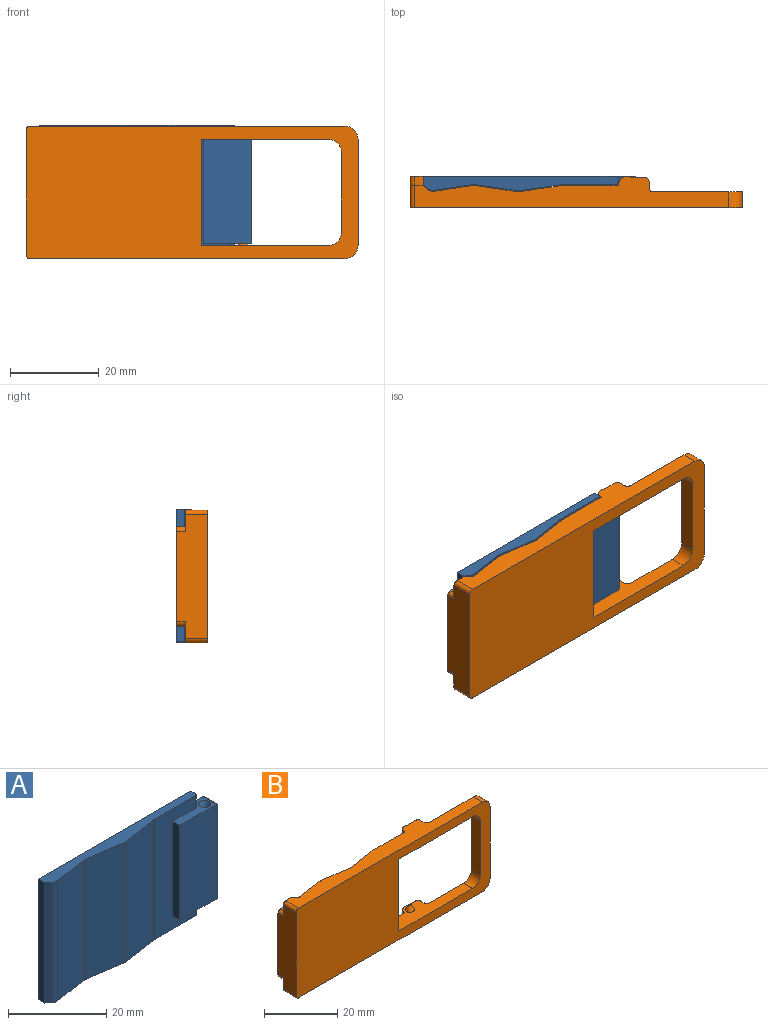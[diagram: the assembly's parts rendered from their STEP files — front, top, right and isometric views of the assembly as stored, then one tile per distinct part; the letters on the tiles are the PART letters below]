
ASSEMBLY  parts=2 mates=1
PART A: 26 faces, bbox 48x3.8x30 mm
  f0: plane 30x11.85mm, normal (0,-1,0), area 202.1mm2, adj f8,f9,f11,f13,f14,f20,f21,f22
  f1: plane 48x30mm, normal (0,1,0), area 1414.3mm2, adj f2,f7,f8,f9,f10,f11,f12,f13
  f2: plane 30x1.8mm, normal (-1,0,0), area 54mm2, adj f1,f3,f8,f9
  f3: plane 30x0.79mm, normal (-0.71,-0.71,0), area 33.4mm2, adj f2,f8,f9,f25
  f4: plane 30x8.71mm, normal (0.15,-0.99,0), area 264.1mm2, adj f8,f9,f24,f25
  f5: plane 30x9.41mm, normal (-0.15,-0.99,0), area 285.4mm2, adj f8,f9,f23,f24
  f6: plane 30x9.56mm, normal (0.15,-0.99,0), area 289.9mm2, adj f8,f9,f22,f23
  f7: plane 22.6x3.8mm, normal (1,0,0), area 85.9mm2, adj f1,f15,f18,f19
  f8: plane 44x3.28mm, normal (0,0,1), area 102.6mm2, adj f0,f1,f2,f3,f4,f5,f6,f10
  f9: plane 44x3.28mm, normal (0,0,-1), area 102.6mm2, adj f0,f1,f2,f3,f4,f5,f6,f12
  f10: plane 3.2x1.3mm, normal (1,0,0), area 4.2mm2, adj f1,f8,f11,f21
  f11: plane 10.5x3.8mm, normal (0,0,1), area 22.4mm2, adj f0,f1,f10,f14,f15,f17,f19,f21
  f12: plane 3.2x1.3mm, normal (1,0,0), area 4.2mm2, adj f1,f9,f13,f20
  f13: plane 10.5x3.8mm, normal (0,0,-1), area 22.4mm2, adj f0,f1,f12,f14,f15,f16,f18,f20
  f14: plane 23.6x2mm, normal (-1,0,0), area 47.2mm2, adj f0,f11,f13,f15
  f15: plane 23.6x11mm, normal (0,-1,0), area 259.5mm2, adj f7,f11,f13,f14,f18,f19
  f16: cone r=1.25mm half-angle=30deg, axis (0,0,-1), area 9.8mm2, adj f13
  f17: cone r=1.25mm half-angle=30deg, axis (0,0,1), area 9.8mm2, adj f11
  f18: cylinder r=0.5mm len=3.8mm, axis (0,-1,0), area 3mm2, adj f1,f7,f13,f15
  f19: cylinder r=0.5mm len=3.8mm, axis (0,-1,0), area 3mm2, adj f1,f7,f11,f15
  f20: cylinder r=0.5mm len=3.2mm, axis (0,0,-1), area 2.5mm2, adj f0,f9,f12,f13
  f21: cylinder r=0.5mm len=3.2mm, axis (0,0,-1), area 2.5mm2, adj f0,f8,f10,f11
  f22: cylinder r=2mm len=30mm, axis (0,0,1), area 8.9mm2, adj f0,f6,f8,f9
  f23: cylinder r=2mm len=30mm, axis (0,0,-1), area 17.9mm2, adj f5,f6,f8,f9
  f24: cylinder r=2mm len=30mm, axis (0,0,1), area 17.9mm2, adj f4,f5,f8,f9
  f25: cylinder r=2mm len=30mm, axis (0,0,-1), area 56.1mm2, adj f3,f4,f8,f9
PART B: 49 faces, bbox 75x7x30 mm
  f0: plane 28.5x7mm, normal (0,0,1), area 128.5mm2, adj f4,f5,f7,f9,f10,f19,f24,f32
  f1: plane 28.5x7mm, normal (0,0,-1), area 128.5mm2, adj f4,f5,f6,f8,f10,f19,f23,f31
  f2: plane 4.75x3mm, normal (0,1,0), area 11.3mm2, adj f11,f14,f15,f26,f27,f40
  f3: plane 4.75x3mm, normal (0,1,0), area 11.3mm2, adj f11,f12,f15,f28,f29,f39
  f4: plane 75x30mm, normal (0,-1,0), area 1493.6mm2, adj f0,f1,f11,f12,f13,f14,f19,f20
  f5: plane 30x12.35mm, normal (0,1,0), area 196.5mm2, adj f0,f1,f6,f7,f12,f14,f19,f45
  f6: cylinder r=2mm len=3mm, axis (0,0,1), area 12.1mm2, adj f1,f5,f12,f33
  f7: cylinder r=2mm len=3mm, axis (0,0,1), area 12.1mm2, adj f0,f5,f14,f34
  f8: plane 3x1.3mm, normal (1,0,0), area 3.9mm2, adj f1,f12,f41,f44
  f9: plane 3x1.3mm, normal (1,0,0), area 3.9mm2, adj f0,f14,f42,f43
  f10: plane 30x20mm, normal (0,1,0), area 210mm2, adj f0,f1,f12,f13,f14,f20,f21,f22
  f11: plane 28x7mm, normal (-1,0,0), area 181mm2, adj f2,f3,f4,f27,f28,f30,f39,f40
  f12: plane 71x7mm, normal (0,0,1), area 316.8mm2, adj f3,f4,f5,f6,f8,f10,f15,f16
  f13: plane 24x3.5mm, normal (1,0,0), area 84mm2, adj f4,f10,f21,f22
  f14: plane 71x7mm, normal (0,0,-1), area 316.8mm2, adj f2,f4,f5,f7,f9,f10,f15,f16
  f15: plane 30x0.79mm, normal (0.71,0.71,0), area 33.4mm2, adj f2,f3,f12,f14,f25,f48
  f16: plane 30x8.71mm, normal (-0.15,0.99,0), area 264.1mm2, adj f12,f14,f47,f48
  f17: plane 30x9.41mm, normal (0.15,0.99,0), area 285.4mm2, adj f12,f14,f46,f47
  f18: plane 30x9.56mm, normal (-0.15,0.99,0), area 289.9mm2, adj f12,f14,f45,f46
  f19: plane 24x5mm, normal (1,0,0), area 120mm2, adj f0,f1,f4,f5
  f20: plane 18x3.5mm, normal (-1,0,0), area 63mm2, adj f4,f10,f23,f24
  f21: cylinder r=3mm len=3.5mm, axis (0,-1,0), area 16.5mm2, adj f4,f10,f13,f14
  f22: cylinder r=3mm len=3.5mm, axis (0,-1,0), area 16.5mm2, adj f4,f10,f12,f13
  f23: cylinder r=3mm len=3.5mm, axis (0,1,0), area 16.5mm2, adj f1,f4,f10,f20
  f24: cylinder r=3mm len=3.5mm, axis (0,1,0), area 16.5mm2, adj f0,f4,f10,f20
  f25: plane 22.5x2mm, normal (1,0,0), area 45mm2, adj f15,f26,f29,f30
  f26: plane 2x2mm, normal (0,0,-1), area 4mm2, adj f2,f25,f27,f30
  f27: cylinder r=1mm len=2mm, axis (0,-1,0), area 3.1mm2, adj f2,f11,f26,f30
  f28: cylinder r=1mm len=2mm, axis (0,-1,0), area 3.1mm2, adj f3,f11,f29,f30
  f29: plane 2x2mm, normal (0,0,1), area 4mm2, adj f3,f25,f28,f30
  f30: plane 22.5x3mm, normal (0,1,0), area 67.1mm2, adj f11,f25,f26,f27,f28,f29
  f31: cone r=1.25mm half-angle=30deg, axis (0,0,1), area 9.1mm2, adj f1,f38
  f32: cone r=1.25mm half-angle=30deg, axis (0,0,-1), area 9.1mm2, adj f0,f37
  f33: plane 3.13x3mm, normal (0,1,0), area 9.4mm2, adj f1,f6,f12,f44
  f34: plane 3.13x3mm, normal (0,1,0), area 9.4mm2, adj f0,f7,f14,f43
  f35: plane 0.35x0.35mm, normal (0,0,1), area 0.1mm2, adj f37
  f36: plane 0.35x0.35mm, normal (0,0,-1), area 0.1mm2, adj f38
  f37: torus R=0.17mm, axis (0,0,-1), area 0.4mm2, adj f32,f35
  f38: torus R=0.17mm, axis (0,0,1), area 0.4mm2, adj f31,f36
  f39: cylinder r=1mm len=5mm, axis (0,-1,0), area 7.9mm2, adj f3,f4,f11,f12
  f40: cylinder r=1mm len=5mm, axis (0,-1,0), area 7.9mm2, adj f2,f4,f11,f14
  f41: cylinder r=1mm len=3mm, axis (0,0,-1), area 4.7mm2, adj f1,f8,f10,f12
  f42: cylinder r=1mm len=3mm, axis (0,0,-1), area 4.7mm2, adj f0,f9,f10,f14
  f43: cylinder r=1mm len=3mm, axis (0,0,1), area 4.7mm2, adj f0,f9,f14,f34
  f44: cylinder r=1mm len=3mm, axis (0,0,1), area 4.7mm2, adj f1,f8,f12,f33
  f45: cylinder r=2mm len=30mm, axis (0,0,1), area 8.9mm2, adj f5,f12,f14,f18
  f46: cylinder r=2mm len=30mm, axis (0,0,-1), area 17.9mm2, adj f12,f14,f17,f18
  f47: cylinder r=2mm len=30mm, axis (0,0,1), area 17.9mm2, adj f12,f14,f16,f17
  f48: cylinder r=2mm len=30mm, axis (0,0,-1), area 56.1mm2, adj f12,f14,f15,f16
PLACE A t=(-119.66,-8.94,16.15)mm
PLACE B t=(-122.66,-15.94,45.95)mm
MATE revolute B.f6 <-> A.f17  axis (0,0,-1) through (-73.66,-10.94,42.95)mm
